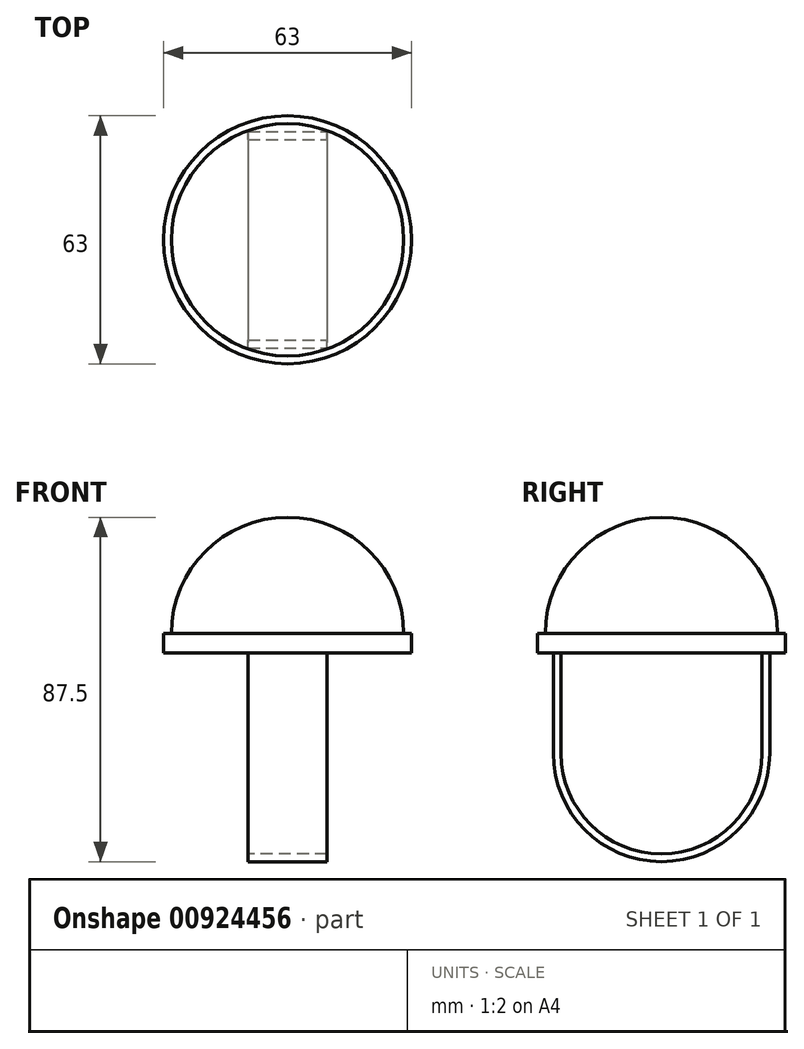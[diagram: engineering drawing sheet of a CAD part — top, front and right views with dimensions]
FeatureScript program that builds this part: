
annotation { "Feature Type Name" : "Feature", "Feature Type Description" : "" }
export const myFeature = defineFeature(function(context is Context, id is Id, definition is map)
    precondition{}
    {
        {
            var Q0;
            Q0=qCreatedBy(makeId("Top.planeOp"),FACE);
            var sketch = newSketch(context, id + "F0", { "sketchPlane" : qUnion([Q0])});
            skCircle(sketch, "E0", {"center": v(0, 0) * mm, "radius": 29.5 * mm});
            skLineSegment(sketch, "E1", {"start": v(0, 29.5) * mm, "end": v(0, -29.5) * mm});
            skSolve(sketch);
        }
        {
            var Q0;
            {var subQ0=sQuery(id+"F0.wireOp",EDGE,"E1");Q0=makeQuery(id+"F0.imprint","IMPRINT",FACE,{"disambiguationData":[TD([[makeQuery(id+"F0.imprint","IMPRINT",EDGE,{"derivedFrom":subQ0}),1.0]])]});}
            var Q1;
            Q1=sQuery(id+"F0.wireOp",EDGE,"E1");
            revolve(context, id + "F1", {"surfaceOperationType" : NewSurfaceOperationType.NEW, "entities" : qUnion([Q0]), "axis" : qUnion([Q1]), "revolveType" : RevolveType.ONE_DIRECTION, "angle" : 180 * degree});
        }
        {
            var Q0;
            Q0=makeQuery(id+"F1.opRevolve","CAP_FACE",FACE,{"disambiguationData":[OSD([sQuery(id+"F0.wireOp",EDGE,"E0"),sQuery(id+"F0.wireOp",EDGE,"E1")])],"isStart":true});
            var sketch = newSketch(context, id + "F2", { "sketchPlane" : qUnion([Q0])});
            skCircle(sketch, "E2", {"center": v(0, 0) * mm, "radius": 31.5 * mm});
            skSolve(sketch);
        }
        {
            var Q0;
            Q0=qSketchRegion(id+"F2",true);
            extrude(context, id + "F3", {"entities" : qUnion([Q0]), "operationType" : NewBodyOperationType.ADD, "depth" : 5 * mm, "offsetDistance" : 25 * mm});
        }
        {
            var Q0;
            Q0=makeQuery(id+"F3.opExtrude","CAP_FACE",FACE,{"disambiguationData":[OSD([sQuery(id+"F2.wireOp",EDGE,"E2")])],"isStart":false});
            var sketch = newSketch(context, id + "F4", { "sketchPlane" : qUnion([Q0])});
            skLineSegment(sketch, "E3.bottom", {"start": v(-10, 27.5) * mm, "end": v(10, 27.5) * mm});
            skLineSegment(sketch, "E3.top", {"start": v(-10, 25.5) * mm, "end": v(10, 25.5) * mm});
            skLineSegment(sketch, "E3.left", {"start": v(-10, 27.5) * mm, "end": v(-10, 25.5) * mm});
            skLineSegment(sketch, "E3.right", {"start": v(10, 27.5) * mm, "end": v(10, 25.5) * mm});
            skLineSegment(sketch, "E4.bottom", {"start": v(-10, -25.5) * mm, "end": v(10, -25.5) * mm});
            skLineSegment(sketch, "E4.top", {"start": v(-10, -27.5) * mm, "end": v(10, -27.5) * mm});
            skLineSegment(sketch, "E4.left", {"start": v(-10, -25.5) * mm, "end": v(-10, -27.5) * mm});
            skLineSegment(sketch, "E4.right", {"start": v(10, -25.5) * mm, "end": v(10, -27.5) * mm});
            skSolve(sketch);
        }
        {
            var Q0;
            Q0=makeQuery(id+"F4.imprint","IMPRINT",FACE,{"disambiguationData":[TD([[makeQuery(id+"F4.imprint","IMPRINT",EDGE,{"derivedFrom":sQuery(id+"F4.wireOp",EDGE,"E3.bottom")}),-1.0]])]});
            var Q1;
            Q1=makeQuery(id+"F4.imprint","IMPRINT",FACE,{"disambiguationData":[TD([[makeQuery(id+"F4.imprint","IMPRINT",EDGE,{"derivedFrom":sQuery(id+"F4.wireOp",EDGE,"E4.bottom")}),-1.0]])]});
            extrude(context, id + "F5", {"entities" : qUnion([Q0, Q1]), "operationType" : NewBodyOperationType.ADD, "depth" : 25.5 * mm, "offsetDistance" : 25 * mm});
        }
        {
            var Q0;
            Q0=makeQuery(id+"F5.opExtrude","CAP_FACE",FACE,{"disambiguationData":[OSD([sQuery(id+"F4.wireOp",EDGE,"E3.bottom"),sQuery(id+"F4.wireOp",EDGE,"E3.top"),sQuery(id+"F4.wireOp",EDGE,"E3.left"),sQuery(id+"F4.wireOp",EDGE,"E3.right")])],"isStart":false});
            var sketch = newSketch(context, id + "F6", { "sketchPlane" : qUnion([Q0])});
            skLineSegment(sketch, "E5", {"start": v(-38.26, 0) * mm, "end": v(53.74, 0) * mm});
            skSolve(sketch);
        }
        {
            var Q0;
            Q0=makeQuery(id+"F6.imprint","IMPRINT",FACE,{"disambiguationData":[TD([[makeQuery(id+"F6.imprint","IMPRINT",EDGE,{"derivedFrom":makeQuery(id+"F5.opExtrude","CAP_EDGE",EDGE,{"disambiguationData":[OSD([sQuery(id+"F4.wireOp",EDGE,"E3.bottom")])],"isStart":false})}),-1.0]])]});
            var Q1;
            Q1=sQuery(id+"F6.wireOp",EDGE,"E5");
            revolve(context, id + "F7", {"operationType" : NewBodyOperationType.ADD, "surfaceOperationType" : NewSurfaceOperationType.NEW, "entities" : qUnion([Q0]), "axis" : qUnion([Q1]), "revolveType" : RevolveType.ONE_DIRECTION, "angle" : 180 * degree});
        }
    });
